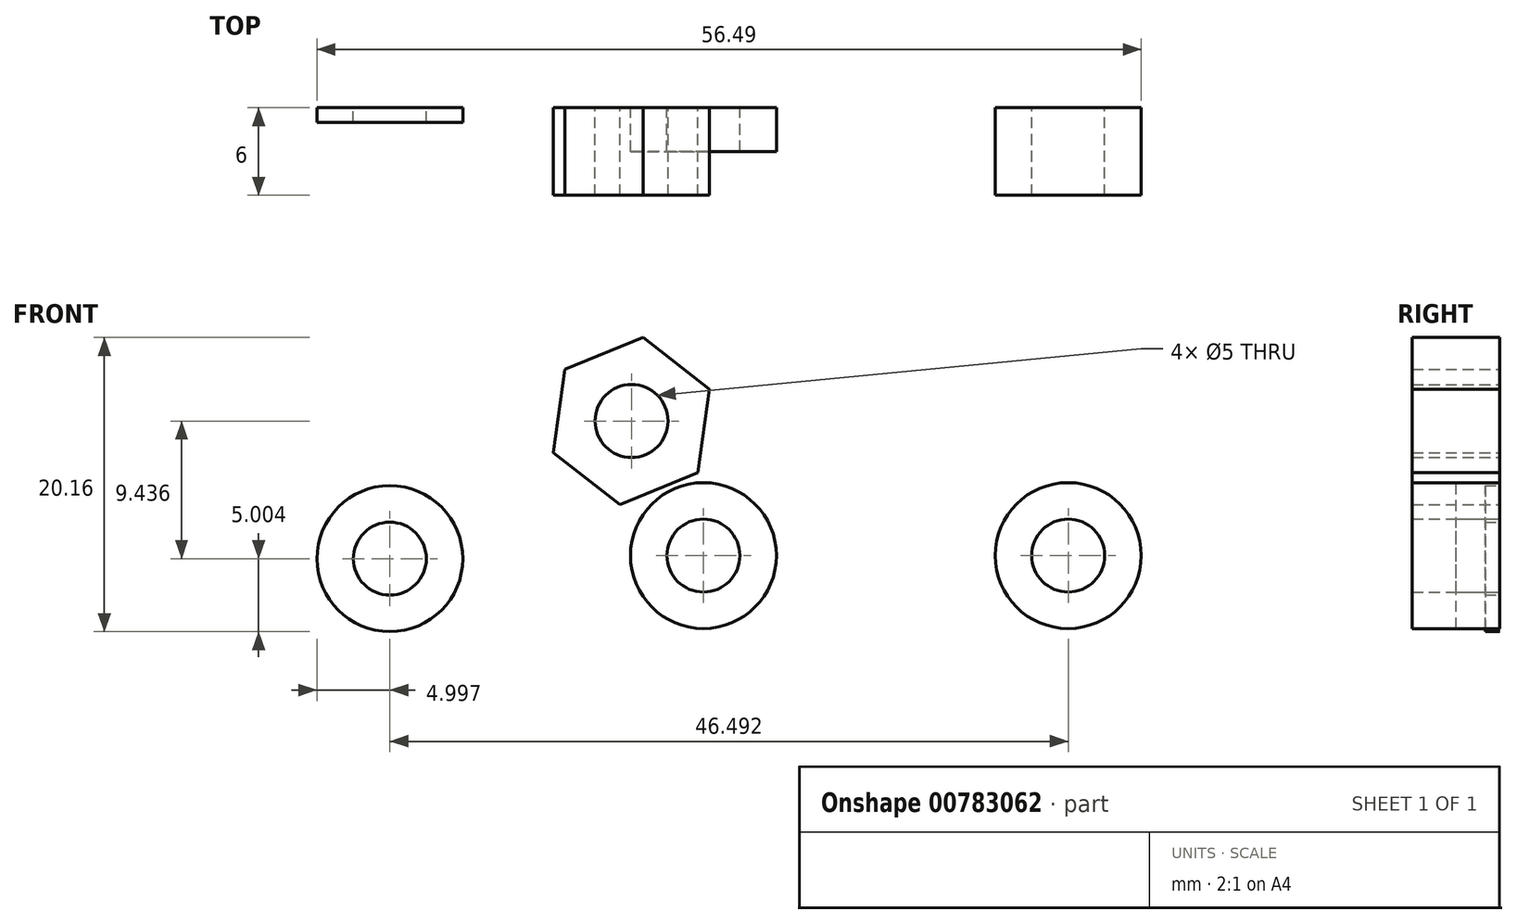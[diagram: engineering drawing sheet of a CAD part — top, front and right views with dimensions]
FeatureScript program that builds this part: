
annotation { "Feature Type Name" : "Feature", "Feature Type Description" : "" }
export const myFeature = defineFeature(function(context is Context, id is Id, definition is map)
    precondition{}
    {
        {
            var Q0;
            Q0=qCreatedBy(makeId("Front.planeOp"),FACE);
            var sketch = newSketch(context, id + "F0", { "sketchPlane" : qUnion([Q0])});
            skCircle(sketch, "E0", {"center": v(3.25, -2.78) * mm, "radius": 5 * mm});
            skCircle(sketch, "E1", {"center": v(3.25, -2.78) * mm, "radius": 2.5 * mm});
            skCircle(sketch, "E2.1.0.0", {"center": v(28.25, -2.78) * mm, "radius": 5 * mm});
            skCircle(sketch, "E2.1.0.1", {"center": v(28.25, -2.78) * mm, "radius": 2.5 * mm});
            skCircle(sketch, "E2.2.0.0", {"center": v(53.25, -2.78) * mm, "radius": 5 * mm});
            skCircle(sketch, "E2.2.0.1", {"center": v(53.25, -2.78) * mm, "radius": 2.5 * mm});
            skLineSegment(sketch, "E2.direction1", {"start": v(3.25, -2.78) * mm, "end": v(28.25, -2.78) * mm, "construction": true});
            skCircle(sketch, "E3.cCircle", {"center": v(-1.68, 6.44) * mm, "radius": 5 * mm, "construction": true});
            skLineSegment(sketch, "E3.0", {"start": v(-0.89, 12.16) * mm, "end": v(3.67, 8.61) * mm});
            skLineSegment(sketch, "E3.1", {"start": v(3.67, 8.61) * mm, "end": v(2.88, 2.9) * mm});
            skLineSegment(sketch, "E3.2", {"start": v(2.88, 2.9) * mm, "end": v(-2.47, 0.72) * mm});
            skLineSegment(sketch, "E3.3", {"start": v(-2.47, 0.72) * mm, "end": v(-7.03, 4.27) * mm});
            skLineSegment(sketch, "E3.4", {"start": v(-7.03, 4.27) * mm, "end": v(-6.24, 9.98) * mm});
            skLineSegment(sketch, "E3.5", {"start": v(-6.24, 9.98) * mm, "end": v(-0.89, 12.16) * mm});
            skPoint(sketch, "E3.0.midPoint", {"position": v(1.4, 10.39) * mm});
            skCircle(sketch, "E4", {"center": v(-1.68, 6.44) * mm, "radius": 2.5 * mm});
            skSolve(sketch);
        }
        {
            var Q0;
            Q0=makeQuery(id+"F0.imprint","IMPRINT",FACE,{"disambiguationData":[TD([[makeQuery(id+"F0.imprint","IMPRINT",EDGE,{"derivedFrom":sQuery(id+"F0.wireOp",EDGE,"E0")}),1.0]])]});
            extrude(context, id + "F1", {"entities" : qUnion([Q0]), "depth" : 3 * mm, "offsetDistance" : 25 * mm});
        }
        {
            var Q0;
            Q0=makeQuery(id+"F0.imprint","IMPRINT",FACE,{"disambiguationData":[TD([[makeQuery(id+"F0.imprint","IMPRINT",EDGE,{"derivedFrom":sQuery(id+"F0.wireOp",EDGE,"E2.1.0.0")}),1.0]])]});
            extrude(context, id + "F2", {"entities" : qUnion([Q0]), "depth" : 6 * mm, "offsetDistance" : 25 * mm});
        }
        {
            var Q0;
            Q0=makeQuery(id+"F0.imprint","IMPRINT",FACE,{"disambiguationData":[TD([[makeQuery(id+"F0.imprint","IMPRINT",EDGE,{"derivedFrom":sQuery(id+"F0.wireOp",EDGE,"E3.0")}),-1.0]])]});
            extrude(context, id + "F3", {"entities" : qUnion([Q0]), "depth" : 6 * mm, "offsetDistance" : 25 * mm});
        }
        {
            var Q0;
            Q0=qCreatedBy(makeId("Front.planeOp"),FACE);
            var sketch = newSketch(context, id + "F4", { "sketchPlane" : qUnion([Q0])});
            skCircle(sketch, "E5", {"center": v(-18.24, -3) * mm, "radius": 5 * mm});
            skCircle(sketch, "E6", {"center": v(-18.24, -3) * mm, "radius": 2.5 * mm});
            skSolve(sketch);
        }
        {
            var Q0;
            Q0=makeQuery(id+"F4.imprint","IMPRINT",FACE,{"disambiguationData":[TD([[makeQuery(id+"F4.imprint","IMPRINT",EDGE,{"derivedFrom":sQuery(id+"F4.wireOp",EDGE,"E5")}),1.0]])]});
            extrude(context, id + "F5", {"entities" : qUnion([Q0]), "depth" : 1 * mm, "offsetDistance" : 25 * mm});
        }
    });
